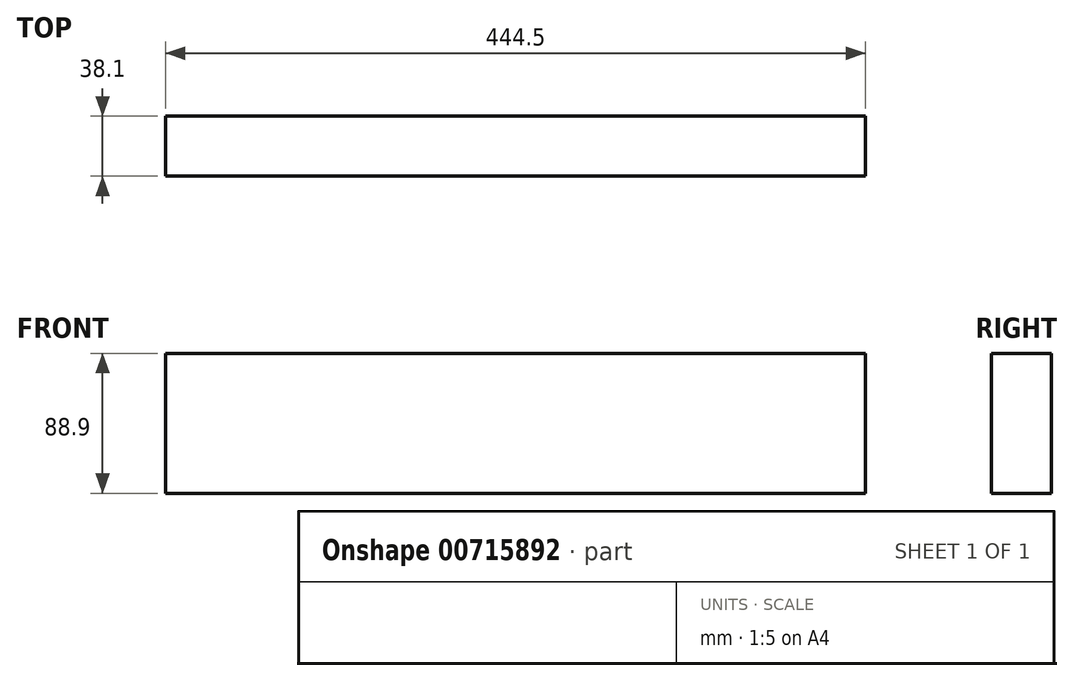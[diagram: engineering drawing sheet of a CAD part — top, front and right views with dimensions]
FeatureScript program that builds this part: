
annotation { "Feature Type Name" : "Feature", "Feature Type Description" : "" }
export const myFeature = defineFeature(function(context is Context, id is Id, definition is map)
    precondition{}
    {
        {
            var Q0;
            Q0=qCreatedBy(makeId("Right.planeOp"),FACE);
            var sketch = newSketch(context, id + "F0", { "sketchPlane" : qUnion([Q0])});
            skLineSegment(sketch, "E0.bottom", {"start": v(-19.05, 44.45) * mm, "end": v(19.05, 44.45) * mm});
            skLineSegment(sketch, "E0.top", {"start": v(-19.05, -44.45) * mm, "end": v(19.05, -44.45) * mm});
            skLineSegment(sketch, "E0.left", {"start": v(-19.05, 44.45) * mm, "end": v(-19.05, -44.45) * mm});
            skLineSegment(sketch, "E0.right", {"start": v(19.05, 44.45) * mm, "end": v(19.05, -44.45) * mm});
            skPoint(sketch, "E0.middle", {"position": v(0, 0) * mm});
            skSolve(sketch);
        }
        {
            var Q0;
            Q0=makeQuery(id+"F0.imprint","IMPRINT",FACE,{"disambiguationData":[TD([[makeQuery(id+"F0.imprint","IMPRINT",EDGE,{"derivedFrom":sQuery(id+"F0.wireOp",EDGE,"E0.bottom")}),-1.0]])]});
            extrude(context, id + "F1", {"entities" : qUnion([Q0]), "depth" : 444.5 * mm, "offsetDistance" : 25.4 * mm, "symmetric" : true});
        }
    });
